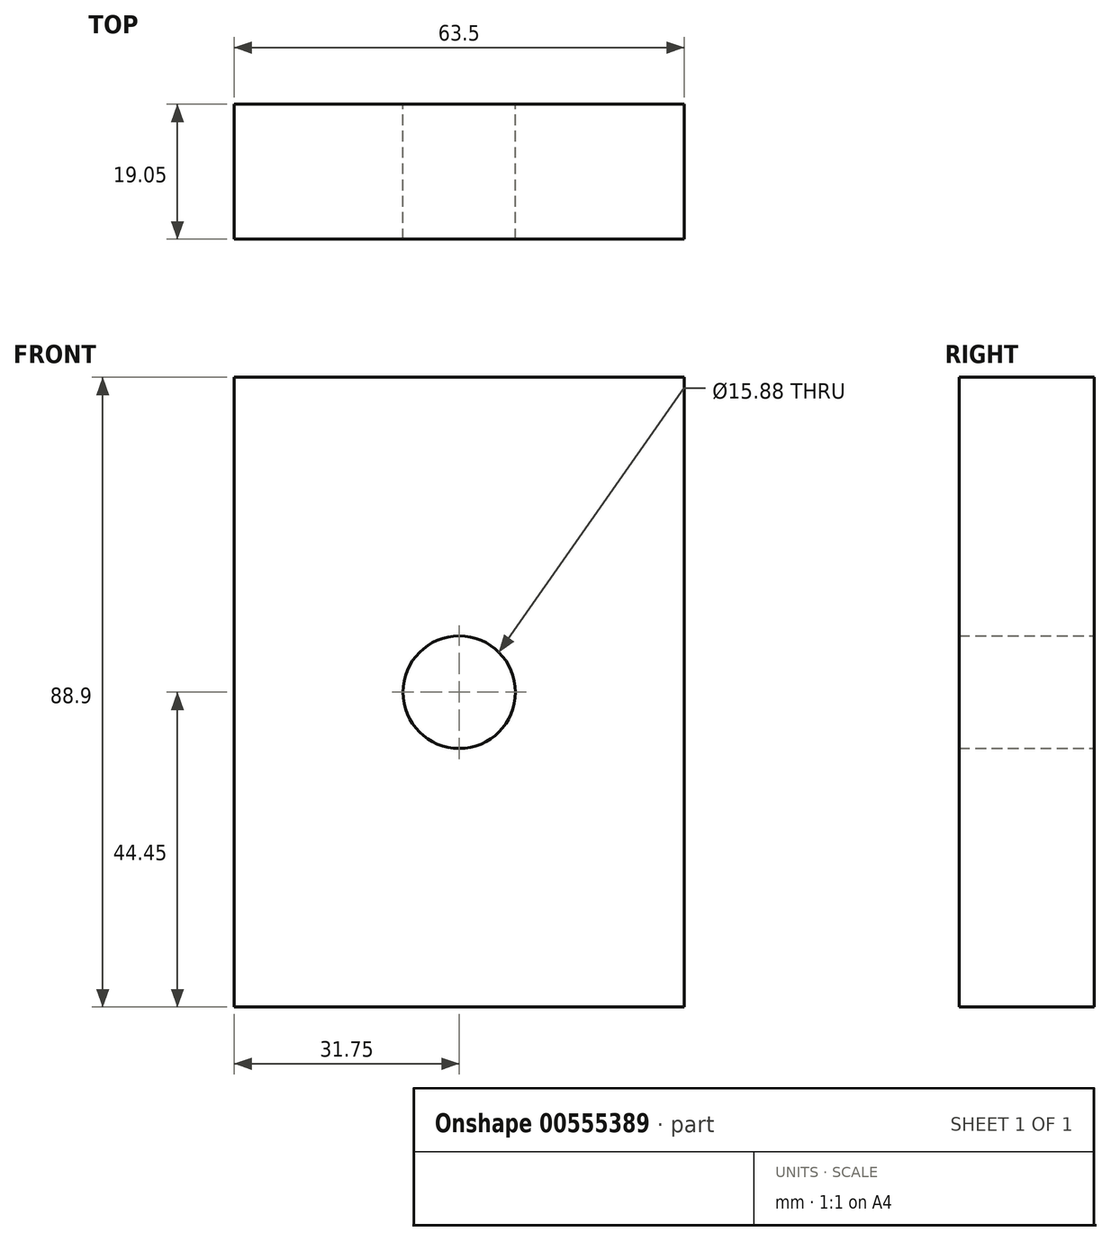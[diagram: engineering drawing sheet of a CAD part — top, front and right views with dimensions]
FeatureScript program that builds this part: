
annotation { "Feature Type Name" : "Feature", "Feature Type Description" : "" }
export const myFeature = defineFeature(function(context is Context, id is Id, definition is map)
    precondition{}
    {
        {
            var Q0;
            Q0=qCreatedBy(makeId("Front.planeOp"),FACE);
            var sketch = newSketch(context, id + "F0", { "sketchPlane" : qUnion([Q0])});
            skLineSegment(sketch, "E0", {"start": v(0, 0) * mm, "end": v(-31.75, 0) * mm});
            skLineSegment(sketch, "E1", {"start": v(-31.75, 0) * mm, "end": v(-31.75, 44.45) * mm});
            skLineSegment(sketch, "E2", {"start": v(0, 44.45) * mm, "end": v(-31.75, 44.45) * mm});
            skLineSegment(sketch, "E3", {"start": v(0, 44.45) * mm, "end": v(31.75, 44.45) * mm});
            skLineSegment(sketch, "E4", {"start": v(31.75, 44.45) * mm, "end": v(31.75, 0) * mm});
            skLineSegment(sketch, "E5", {"start": v(31.75, 0) * mm, "end": v(31.75, -44.45) * mm});
            skLineSegment(sketch, "E6", {"start": v(31.75, -44.45) * mm, "end": v(0, -44.45) * mm});
            skLineSegment(sketch, "E7", {"start": v(0, -44.45) * mm, "end": v(-31.75, -44.45) * mm});
            skLineSegment(sketch, "E8", {"start": v(-31.75, -44.45) * mm, "end": v(-31.75, 0) * mm});
            skSolve(sketch);
        }
        {
            var Q0;
            Q0=makeQuery(id+"F0.imprint","IMPRINT",FACE,{"disambiguationData":[TD([[makeQuery(id+"F0.imprint","IMPRINT",EDGE,{"derivedFrom":sQuery(id+"F0.wireOp",EDGE,"E1")}),-1.0]])]});
            var sketch = newSketch(context, id + "F1", { "sketchPlane" : qUnion([Q0])});
            skPoint(sketch, "E9", {"position": v(0, 0) * mm});
            skCircle(sketch, "E10", {"center": v(0, 0) * mm, "radius": 7.94 * mm});
            skSolve(sketch);
        }
        {
            var Q0;
            Q0=makeQuery(id+"F1.imprint","IMPRINT",FACE,{"disambiguationData":[TD([[makeQuery(id+"F1.imprint","IMPRINT",EDGE,{"derivedFrom":sQuery(id+"F1.wireOp",EDGE,"E10")}),-1.0]])]});
            extrude(context, id + "F2", {"entities" : qUnion([Q0]), "depth" : 19.05 * mm, "offsetDistance" : 25.4 * mm});
        }
    });
